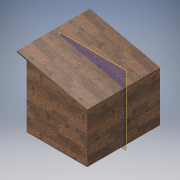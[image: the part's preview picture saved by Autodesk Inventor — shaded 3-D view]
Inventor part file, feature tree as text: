
AUTODESK INVENTOR PART (.ipt)
format: ipt  version: 2017 (Build 210142000, 142)  size: 294,400 bytes
history: native  units: in
note: dims shown in document units (in); Inventor stores cm internally (conversion verified against a paired STEP export)
features: extrude x11, sketch x11, projected_geometry x9, plane x1, mirror x1
ambient origin geometry x8: Origin, YZ Plane, XZ Plane, XY Plane, X Axis, Y Axis, Z Axis, Center Point
bodies: Solid1 (feature_tree)
feature tree (33):
  extrude  "Extrusion1"  Depth=36.0in
  extrude  "Extrusion5"  Depth=0.75in
  extrude  "Extrusion7"  Depth=0.75in
  extrude  "Extrusion8"  TaperAngle=90.0deg  [1 undecoded]
  plane  "Work Plane2"
  mirror  "Mirror1"
  extrude  "Extrusion9"  Depth=24.0in TaperAngle=0.0deg
  extrude  "Extrusion10"  Depth=0.75in
  extrude  "Extrusion11"  Depth=18.0in TaperAngle=0.0deg
  extrude  "Extrusion12"  Depth=0.75in TaperAngle=0.0deg
  extrude  "Extrusion13"  Depth=0.75in
  extrude  "Extrusion14"  Depth=0.75in
  extrude  "Extrusion15"  Depth=5.0in TaperAngle=0.0deg
  sketch  "Sketch1"  dims[d0=30.0in d1=36.0in]
  sketch  "Sketch5"  dims[d2=0.75in d3=0.0in d22=6.0in]
  projected_geometry  "Projected Loop4"
  sketch  "Sketch7"  dims[d23=0.0871in d25=0.75in]
  projected_geometry  "Projected Loop7"
  sketch  "Sketch8"  dims[d26=90.0deg d28=90.0deg]
  projected_geometry  "Projected Loop8"
  sketch  "Sketch9"  dims[d29=90.0deg d30=24.0in d31=0.0in]
  projected_geometry  "Projected Loop9"
  sketch  "Sketch12"  dims[d38=0.75in d39=0.75in]
  projected_geometry  "Projected Loop13"
  sketch  "Sketch13"  dims[d40=18.0in d41=24.0in d42=0.0in]
  projected_geometry  "Projected Loop14"
  sketch  "Sketch14"  dims[d43=0.75in d44=0.0in d45=0.75in d46=0.0in]
  projected_geometry  "Projected Loop15"
  sketch  "Sketch15"  dims[d57=0.75in d58=6.0in]
  projected_geometry  "Projected Loop16"
  sketch  "Sketch16"  dims[d59=1.0in d60=0.0in d61=0.75in]
  projected_geometry  "Projected Loop17"
  sketch  "Sketch17"  dims[d62=1.0in d63=0.0in d64=5.0in d65=0.0in d66=0.75in d67=5.0in d68=0.0in d69=0.75in d70=5.0in d71=0.75in d72=5.0in d73=5.0in d74=0.0in d75=0.75in d76=5.0in d77=0.0in]
note: 1 required parameter value undecoded (feature->parameter linkage not recoverable at this tier; creation-order binding heuristic only, values carry confidence <= 0.55)
